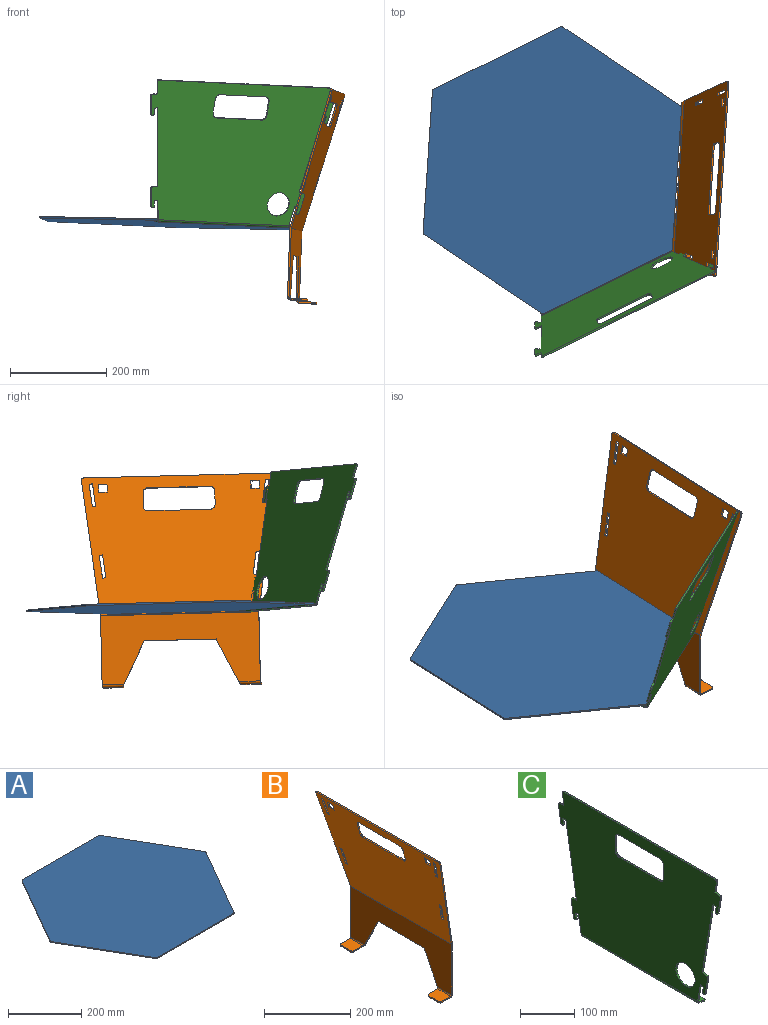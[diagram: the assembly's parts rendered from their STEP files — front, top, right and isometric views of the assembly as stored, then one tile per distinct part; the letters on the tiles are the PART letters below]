
ASSEMBLY  parts=3 mates=3
PART A: 14 faces, bbox 598.5x519.6x3 mm
  f0: plane 294.23x3mm, normal (0,-1,0), area 882.7mm2, adj f6,f7,f8,f13
  f1: plane 254.81x147.11mm, normal (0.87,-0.5,0), area 882.7mm2, adj f6,f7,f8,f9
  f2: plane 254.81x147.11mm, normal (0.87,0.5,0), area 882.7mm2, adj f6,f7,f9,f10
  f3: plane 294.23x3mm, normal (0,1,0), area 882.7mm2, adj f6,f7,f10,f11
  f4: plane 254.81x147.11mm, normal (-0.87,0.5,0), area 882.7mm2, adj f6,f7,f11,f12
  f5: plane 254.81x147.11mm, normal (-0.87,-0.5,0), area 882.7mm2, adj f6,f7,f12,f13
  f6: plane 598.45x519.62mm, normal (0,0,1), area 233818.8mm2, adj f0,f1,f2,f3,f4,f5,f8,f9
  f7: plane 598.45x519.62mm, normal (0,0,-1), area 233818.8mm2, adj f0,f1,f2,f3,f4,f5,f8,f9
  f8: cylinder r=5mm len=4.33mm, axis (0,0,-1), area 15.7mm2, adj f0,f1,f6,f7
  f9: cylinder r=5mm len=5mm, axis (0,0,-1), area 15.7mm2, adj f1,f2,f6,f7
  f10: cylinder r=5mm len=4.33mm, axis (0,0,-1), area 15.7mm2, adj f2,f3,f6,f7
  f11: cylinder r=5mm len=4.33mm, axis (0,0,-1), area 15.7mm2, adj f3,f4,f6,f7
  f12: cylinder r=5mm len=5mm, axis (0,0,-1), area 15.7mm2, adj f4,f5,f6,f7
  f13: cylinder r=5mm len=4.33mm, axis (0,0,-1), area 15.7mm2, adj f0,f5,f6,f7
PART B: 72 faces, bbox 80.7x407x439.8 mm
  f0: plane 150x3.18mm, normal (0,0,-1), area 476.3mm2, adj f1,f4,f5,f6
  f1: plane 89.53x44.76mm, normal (0,0.89,-0.45), area 317.8mm2, adj f0,f5,f6,f58
  f2: plane 143.8x3.18mm, normal (0,-1,0), area 456.6mm2, adj f5,f6,f46,f57
  f3: plane 143.8x3.18mm, normal (0,1,0), area 456.6mm2, adj f5,f6,f47,f69
  f4: plane 89.53x44.76mm, normal (0,-0.89,-0.45), area 317.8mm2, adj f0,f5,f6,f68
  f5: plane 330x143.8mm, normal (-1,0,0), area 30019.3mm2, adj f0,f1,f2,f3,f4,f49,f60,f71
  f6: plane 330x143.8mm, normal (1,0,0), area 30019.3mm2, adj f0,f1,f2,f3,f4,f48,f59,f70
  f7: plane 407.03x289.08mm, normal (0.97,0,0.26), area 101115mm2, adj f8,f10,f11,f12,f13,f14,f15,f16
  f8: plane 284.45x79.06mm, normal (0.03,-0.99,-0.13), area 940.2mm2, adj f7,f9,f45,f46
  f9: plane 407.03x289.08mm, normal (-0.97,0,-0.26), area 101115mm2, adj f8,f10,f11,f12,f13,f14,f15,f16
  f10: plane 284.45x79.06mm, normal (0.03,0.99,-0.13), area 940.2mm2, adj f7,f9,f44,f47
  f11: plane 130x3.07mm, normal (0.26,0,-0.97), area 412.7mm2, adj f7,f9,f12,f43
  f12: cylinder r=10mm len=10.48mm, axis (-0.97,0,-0.26), area 49.9mm2, adj f7,f9,f11,f13
  f13: plane 29.8x10.83mm, normal (0,1,0), area 95.2mm2, adj f7,f9,f12,f14
  f14: cylinder r=10mm len=10.48mm, axis (-0.97,0,-0.26), area 49.9mm2, adj f7,f9,f13,f15
  f15: plane 130x3.07mm, normal (-0.26,0,0.97), area 412.8mm2, adj f7,f9,f14,f16
  f16: cylinder r=10mm len=10.48mm, axis (-0.97,0,-0.26), area 49.9mm2, adj f7,f9,f15,f17
  f17: plane 29.8x10.83mm, normal (0,-1,0), area 95.3mm2, adj f7,f9,f16,f43
  f18: plane 48.71x15.9mm, normal (-0.03,0.99,0.13), area 158.7mm2, adj f7,f9,f19,f42
  f19: plane 6.94x3.3mm, normal (-0.26,-0.13,0.96), area 22.2mm2, adj f7,f9,f18,f20
  f20: plane 48.71x15.9mm, normal (0.03,-0.99,-0.13), area 158.8mm2, adj f7,f9,f19,f42
  f21: plane 17.24x7.47mm, normal (0,-1,0), area 54mm2, adj f7,f9,f22,f41
  f22: plane 17x3.07mm, normal (0.26,0,-0.97), area 54mm2, adj f7,f9,f21,f23
  f23: plane 17.24x7.47mm, normal (0,1,0), area 54mm2, adj f7,f9,f22,f41
  f24: plane 48.71x15.9mm, normal (0.03,-0.99,-0.13), area 158.8mm2, adj f7,f9,f25,f40
  f25: plane 6.94x3.3mm, normal (0.26,0.13,-0.96), area 22.2mm2, adj f7,f9,f24,f26
  f26: plane 48.71x15.9mm, normal (-0.03,0.99,0.13), area 158.7mm2, adj f7,f9,f25,f40
  f27: plane 17.24x7.47mm, normal (0,-1,0), area 54mm2, adj f7,f9,f28,f39
  f28: plane 17x3.07mm, normal (0.26,0,-0.97), area 54mm2, adj f7,f9,f27,f29
  f29: plane 17.24x7.47mm, normal (0,1,0), area 54mm2, adj f7,f9,f28,f39
  f30: plane 6.94x3.3mm, normal (0.26,-0.13,-0.96), area 22.2mm2, adj f7,f9,f31,f38
  f31: plane 48.71x15.9mm, normal (0.03,0.99,-0.13), area 158.8mm2, adj f7,f9,f30,f32
  f32: plane 6.94x3.3mm, normal (-0.26,0.13,0.96), area 22.2mm2, adj f7,f9,f31,f38
  f33: plane 48.71x15.9mm, normal (-0.03,-0.99,0.13), area 158.7mm2, adj f7,f9,f34,f37
  f34: plane 6.94x3.3mm, normal (0.26,-0.13,-0.96), area 22.2mm2, adj f7,f9,f33,f35
  f35: plane 48.71x15.9mm, normal (0.03,0.99,-0.13), area 158.8mm2, adj f7,f9,f34,f37
  f36: plane 397.03x3.07mm, normal (-0.26,0,0.97), area 1260.6mm2, adj f7,f9,f44,f45
  f37: plane 6.94x3.3mm, normal (-0.26,0.13,0.96), area 22.2mm2, adj f7,f9,f33,f35
  f38: plane 48.71x15.9mm, normal (-0.03,-0.99,0.13), area 158.7mm2, adj f7,f9,f30,f32
  f39: plane 17x3.07mm, normal (-0.26,0,0.97), area 54mm2, adj f7,f9,f27,f29
  f40: plane 6.94x3.3mm, normal (-0.26,-0.13,0.96), area 22.2mm2, adj f7,f9,f24,f26
  f41: plane 17x3.07mm, normal (-0.26,0,0.97), area 54mm2, adj f7,f9,f21,f23
  f42: plane 6.94x3.3mm, normal (0.26,0.13,-0.96), area 22.2mm2, adj f7,f9,f18,f20
  f43: cylinder r=10mm len=10.48mm, axis (-0.97,0,-0.26), area 49.9mm2, adj f7,f9,f11,f17
  f44: cylinder r=5mm len=6.28mm, axis (0.97,0,0.26), area 27mm2, adj f7,f9,f10,f36
  f45: cylinder r=5mm len=6.28mm, axis (0.97,0,0.26), area 27mm2, adj f7,f8,f9,f36
  f46: bspline ~3.25x1.42mm, area 3.2mm2, adj f2,f8,f48,f49
  f47: bspline ~3.25x1.42mm, area 3.2mm2, adj f3,f10,f48,f49
  f48: cylinder r=5.47mm len=330.16mm, axis (0,-1,0), area 473.1mm2, adj f6,f7,f46,f47
  f49: cylinder r=2.3mm len=330.16mm, axis (0,-1,0), area 198.8mm2, adj f5,f9,f46,f47
  f50: plane 32.5x3.18mm, normal (-1,0,0), area 103.2mm2, adj f53,f54,f55,f56
  f51: plane 29.53x3.18mm, normal (0,-1,0), area 93.7mm2, adj f53,f54,f55,f57
  f52: plane 29.53x3.18mm, normal (0,1,0), area 93.7mm2, adj f53,f54,f56,f58
  f53: plane 42.5x34.53mm, normal (0,0,1), area 1456.6mm2, adj f50,f51,f52,f55,f56,f60
  f54: plane 42.5x34.53mm, normal (0,0,-1), area 1456.6mm2, adj f50,f51,f52,f55,f56,f59
  f55: cylinder r=5mm len=5mm, axis (0,0,1), area 24.9mm2, adj f50,f51,f53,f54
  f56: cylinder r=5mm len=5mm, axis (0,0,1), area 24.9mm2, adj f50,f52,f53,f54
  f57: plane 5.48x5.48mm, normal (0,-1,0), area 19.4mm2, adj f2,f51,f59,f60
  f58: bspline ~5.48x5.48mm, area 21.7mm2, adj f1,f52,f59,f60
  f59: cylinder r=5.47mm len=45.24mm, axis (0,-1,0), area 374mm2, adj f6,f54,f57,f58
  f60: cylinder r=2.3mm len=45.24mm, axis (0,-1,0), area 157.1mm2, adj f5,f53,f57,f58
  f61: plane 29.53x3.18mm, normal (0,1,0), area 93.7mm2, adj f64,f65,f67,f69
  f62: plane 32.5x3.18mm, normal (-1,0,0), area 103.2mm2, adj f64,f65,f66,f67
  f63: plane 29.53x3.18mm, normal (0,-1,0), area 93.7mm2, adj f64,f65,f66,f68
  f64: plane 42.5x34.53mm, normal (0,0,1), area 1456.6mm2, adj f61,f62,f63,f66,f67,f71
  f65: plane 42.5x34.53mm, normal (0,0,-1), area 1456.6mm2, adj f61,f62,f63,f66,f67,f70
  f66: cylinder r=5mm len=5mm, axis (0,0,1), area 24.9mm2, adj f62,f63,f64,f65
  f67: cylinder r=5mm len=5mm, axis (0,0,1), area 24.9mm2, adj f61,f62,f64,f65
  f68: bspline ~5.48x5.48mm, area 21.7mm2, adj f4,f63,f70,f71
  f69: plane 5.48x5.48mm, normal (0,1,0), area 19.4mm2, adj f3,f61,f70,f71
  f70: cylinder r=5.47mm len=45.24mm, axis (0,-1,0), area 374.1mm2, adj f6,f65,f68,f69
  f71: cylinder r=2.3mm len=45.24mm, axis (0,-1,0), area 157.1mm2, adj f5,f64,f68,f69
PART C: 63 faces, bbox 22.5x422.1x308.2 mm
  f0: plane 30x3.18mm, normal (0,-1,0), area 95.2mm2, adj f1,f35,f36,f37
  f1: cylinder r=10mm len=10mm, axis (-1,0,0), area 49.9mm2, adj f0,f2,f36,f37
  f2: plane 105x3.18mm, normal (0,0,-1), area 333.4mm2, adj f1,f3,f36,f37
  f3: cylinder r=10mm len=10mm, axis (-1,0,0), area 49.9mm2, adj f2,f4,f36,f37
  f4: plane 30x3.18mm, normal (0,1,0), area 95.2mm2, adj f3,f5,f36,f37
  f5: cylinder r=10mm len=10mm, axis (-1,0,0), area 49.9mm2, adj f4,f6,f36,f37
  f6: plane 105x3.18mm, normal (0,0,1), area 333.4mm2, adj f5,f35,f36,f37
  f7: plane 11.84x3.18mm, normal (0,0.17,0.99), area 38.1mm2, adj f34,f36,f37,f50
  f8: plane 38.46x6.45mm, normal (0,0.99,-0.17), area 123.8mm2, adj f36,f37,f43,f50
  f9: plane 3.18x0.99mm, normal (0,-0.17,-0.99), area 3.2mm2, adj f36,f37,f40,f43
  f10: plane 11.84x3.18mm, normal (0,-0.99,0.17), area 38.1mm2, adj f11,f36,f37,f40
  f11: plane 7.89x3.18mm, normal (0,-0.17,-0.99), area 25.4mm2, adj f10,f12,f36,f37
  f12: plane 167.66x28.1mm, normal (0,0.99,-0.17), area 539.8mm2, adj f11,f13,f36,f37
  f13: plane 11.84x3.18mm, normal (0,0.17,0.99), area 38.1mm2, adj f12,f36,f37,f51
  f14: plane 38.46x6.45mm, normal (0,0.99,-0.17), area 123.8mm2, adj f36,f37,f49,f51
  f15: plane 3.18x0.99mm, normal (0,-0.17,-0.99), area 3.2mm2, adj f36,f37,f48,f49
  f16: plane 11.84x3.18mm, normal (0,-0.99,0.17), area 38.1mm2, adj f17,f36,f37,f48
  f17: plane 7.89x3.18mm, normal (0,-0.17,-0.99), area 25.4mm2, adj f16,f18,f36,f37
  f18: plane 41.88x7.02mm, normal (0,0.99,-0.17), area 134.8mm2, adj f17,f36,f37,f60
  f19: plane 41.88x7.02mm, normal (0,-0.99,-0.17), area 134.8mm2, adj f20,f36,f37,f59
  f20: plane 7.89x3.18mm, normal (0,0.17,-0.99), area 25.4mm2, adj f19,f21,f36,f37
  f21: plane 11.84x3.18mm, normal (0,0.99,0.17), area 38.1mm2, adj f20,f36,f37,f38
  f22: plane 3.18x0.99mm, normal (0,0.17,-0.99), area 3.2mm2, adj f36,f37,f38,f41
  f23: plane 38.46x6.45mm, normal (0,-0.99,-0.17), area 123.8mm2, adj f36,f37,f41,f46
  f24: plane 11.84x3.18mm, normal (0,-0.17,0.99), area 38.1mm2, adj f25,f36,f37,f46
  f25: plane 167.66x28.1mm, normal (0,-0.99,-0.17), area 539.8mm2, adj f24,f26,f36,f37
  f26: plane 7.89x3.18mm, normal (0,0.17,-0.99), area 25.4mm2, adj f25,f27,f36,f37
  f27: plane 11.84x3.18mm, normal (0,0.99,0.17), area 38.1mm2, adj f26,f36,f37,f42
  f28: plane 3.18x0.99mm, normal (0,0.17,-0.99), area 3.2mm2, adj f36,f37,f39,f42
  f29: plane 38.46x6.45mm, normal (0,-0.99,-0.17), area 123.8mm2, adj f36,f37,f39,f47
  f30: plane 11.84x3.18mm, normal (0,-0.17,0.99), area 38.1mm2, adj f31,f36,f37,f47
  f31: plane 26.02x4.36mm, normal (0,-0.99,-0.17), area 83.8mm2, adj f30,f36,f37,f44
  f32: plane 396.23x3.18mm, normal (0,0,1), area 1258mm2, adj f36,f37,f44,f45
  f33: cylinder r=25mm len=50mm, axis (-1,0,0), area 498.7mm2, adj f36,f37
  f34: plane 26.02x4.36mm, normal (0,0.99,-0.17), area 83.8mm2, adj f7,f36,f37,f45
  f35: cylinder r=10mm len=10mm, axis (-1,0,0), area 49.9mm2, adj f0,f6,f36,f37
  f36: plane 422.11x298.24mm, normal (-1,0,0), area 99441.4mm2, adj f0,f1,f2,f3,f4,f5,f6,f7
  f37: plane 422.11x298.24mm, normal (1,0,0), area 99441.4mm2, adj f0,f1,f2,f3,f4,f5,f6,f7
  f38: cylinder r=3mm len=3.45mm, axis (-1,0,0), area 15mm2, adj f21,f22,f36,f37
  f39: cylinder r=3mm len=3.45mm, axis (-1,0,0), area 15mm2, adj f28,f29,f36,f37
  f40: cylinder r=3mm len=3.45mm, axis (-1,0,0), area 15mm2, adj f9,f10,f36,f37
  f41: cylinder r=3mm len=3.45mm, axis (-1,0,0), area 15mm2, adj f22,f23,f36,f37
  f42: cylinder r=3mm len=3.45mm, axis (-1,0,0), area 15mm2, adj f27,f28,f36,f37
  f43: cylinder r=3mm len=3.45mm, axis (-1,0,0), area 15mm2, adj f8,f9,f36,f37
  f44: cylinder r=3mm len=3.5mm, axis (1,0,0), area 16.5mm2, adj f31,f32,f36,f37
  f45: cylinder r=3mm len=3.5mm, axis (1,0,0), area 16.5mm2, adj f32,f34,f36,f37
  f46: cylinder r=3mm len=3.45mm, axis (-1,0,0), area 15mm2, adj f23,f24,f36,f37
  f47: cylinder r=3mm len=3.45mm, axis (-1,0,0), area 15mm2, adj f29,f30,f36,f37
  f48: cylinder r=3mm len=3.45mm, axis (-1,0,0), area 15mm2, adj f15,f16,f36,f37
  f49: cylinder r=3mm len=3.45mm, axis (-1,0,0), area 15mm2, adj f14,f15,f36,f37
  f50: cylinder r=3mm len=3.45mm, axis (-1,0,0), area 15mm2, adj f7,f8,f36,f37
  f51: cylinder r=3mm len=3.45mm, axis (-1,0,0), area 15mm2, adj f13,f14,f36,f37
  f52: plane 294.25x3.07mm, normal (0.97,0,-0.26), area 934.2mm2, adj f55,f56,f57,f58
  f53: plane 15.66x7.04mm, normal (0.04,-1,-0.01), area 48.8mm2, adj f55,f56,f57,f59
  f54: plane 15.66x7.04mm, normal (0.04,1,-0.01), area 48.8mm2, adj f55,f56,f58,f60
  f55: plane 301.58x17.61mm, normal (-0.26,0,-0.97), area 5481.4mm2, adj f52,f53,f54,f57,f58,f61
  f56: plane 301.58x17.61mm, normal (0.26,0,0.97), area 5481.4mm2, adj f52,f53,f54,f57,f58,f62
  f57: cylinder r=3mm len=3.81mm, axis (-0.26,0,-0.97), area 14.5mm2, adj f52,f53,f55,f56
  f58: cylinder r=3mm len=3.81mm, axis (-0.26,0,-0.97), area 14.5mm2, adj f52,f54,f55,f56
  f59: bspline ~5.29x4.88mm, area 16.4mm2, adj f19,f53,f61,f62
  f60: bspline ~5.29x4.88mm, area 16.5mm2, adj f18,f54,f61,f62
  f61: cylinder r=5.47mm len=303.35mm, axis (0,-1,0), area 2167.7mm2, adj f36,f55,f59,f60
  f62: cylinder r=2.3mm len=303.35mm, axis (0,-1,0), area 910.6mm2, adj f37,f56,f59,f60
PLACE A rot(axis=(0.01,0.03,1),86.2deg) t=(-17.1,6.76,-10.38)mm fixed
PLACE B rot(axis=(0.02,0.01,1),176.2deg) t=(272.98,-276.72,128.28)mm
PLACE C rot(axis=(0.14,-0.06,0.99),116.5deg) t=(-117.18,-376.36,147.02)mm
MATE planar C.f56 <-> A.f7  axis (0.03,0.02,1) through (91.17,-219.37,-8.92)mm
MATE parallel A.f0 <-> B.f6  axis (1,-0.07,-0.03) through (242.04,-10.54,-17.53)mm
MATE parallel B.f54 <-> A.f7  axis (-0.03,-0.02,-1) through (273.45,125.26,-176.2)mm
